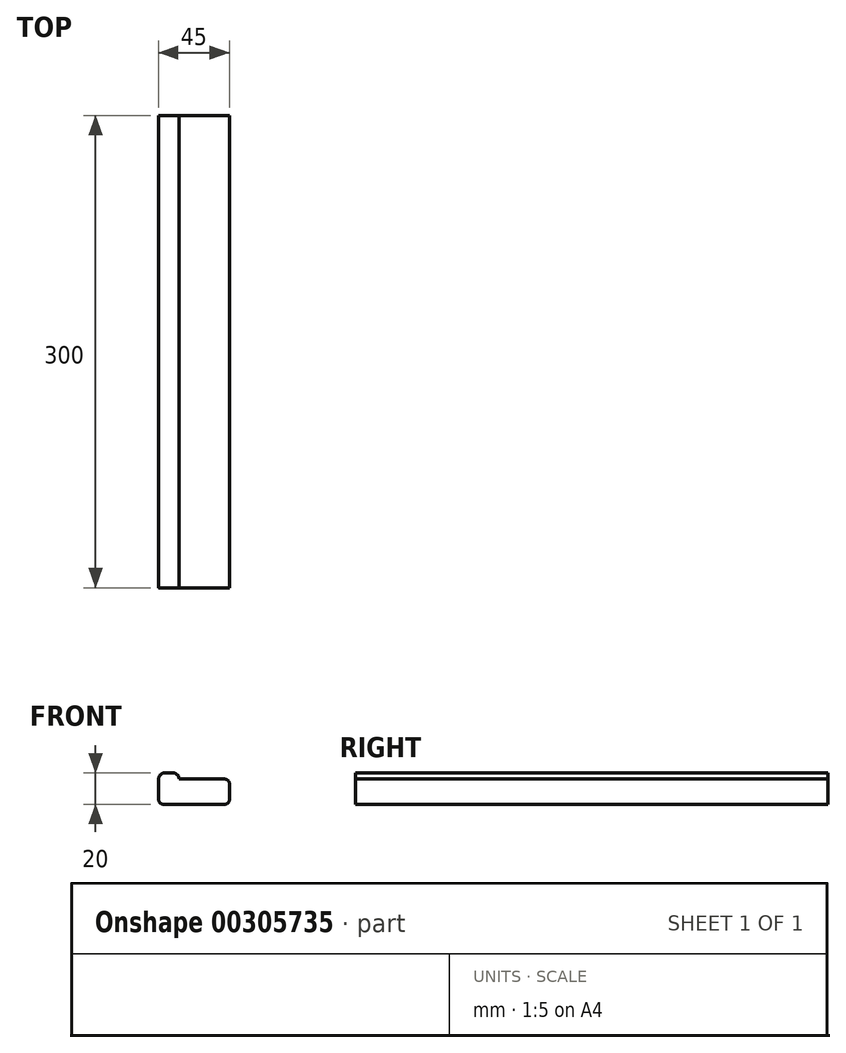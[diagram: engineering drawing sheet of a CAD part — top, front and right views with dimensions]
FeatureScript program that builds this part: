
annotation { "Feature Type Name" : "Feature", "Feature Type Description" : "" }
export const myFeature = defineFeature(function(context is Context, id is Id, definition is map)
    precondition{}
    {
        {
            var Q0;
            Q0=qCreatedBy(makeId("Front.planeOp"),FACE);
            var sketch = newSketch(context, id + "F0", { "sketchPlane" : qUnion([Q0])});
            skLineSegment(sketch, "E0.bottom", {"start": v(3, 0) * mm, "end": v(42, 0) * mm});
            skLineSegment(sketch, "E0.top", {"start": v(13, 16) * mm, "end": v(42, 16) * mm});
            skLineSegment(sketch, "E0.left", {"start": v(0, 3) * mm, "end": v(0, 16) * mm});
            skLineSegment(sketch, "E0.right", {"start": v(45, 3) * mm, "end": v(45, 13) * mm});
            skArc(sketch, "E1", {"start": v(4, 20) * mm, "mid": v(1.17, 18.83) * mm, "end": v(0, 16) * mm});
            skArc(sketch, "E2", {"start": v(13, 16) * mm, "mid": v(11.83, 18.83) * mm, "end": v(9, 20) * mm});
            skLineSegment(sketch, "E3", {"start": v(4, 20) * mm, "end": v(9, 20) * mm});
            skPoint(sketch, "E4.visualSharp", {"position": v(0, 0) * mm});
            skArc(sketch, "E4.filletArc", {"start": v(0, 3) * mm, "mid": v(0.88, 0.88) * mm, "end": v(3, 0) * mm});
            skPoint(sketch, "E5.visualSharp", {"position": v(45, 0) * mm});
            skArc(sketch, "E5.filletArc", {"start": v(42, 0) * mm, "mid": v(44.12, 0.88) * mm, "end": v(45, 3) * mm});
            skPoint(sketch, "E6.visualSharp", {"position": v(45, 16) * mm});
            skArc(sketch, "E6.filletArc", {"start": v(45, 13) * mm, "mid": v(44.12, 15.12) * mm, "end": v(42, 16) * mm});
            skSolve(sketch);
        }
        {
            var Q0;
            Q0 = qSketchRegion(id + "F0", true);
            extrude(context, id + "F1", {"entities" : qUnion([Q0]), "depth" : 300 * mm});
        }
    });
